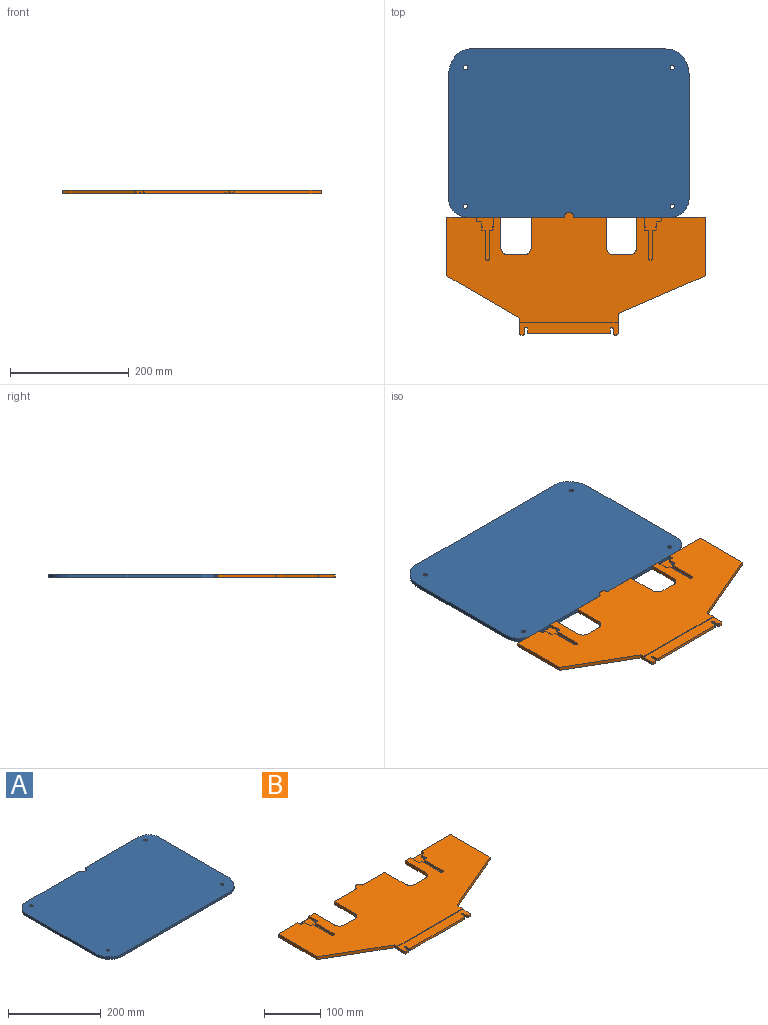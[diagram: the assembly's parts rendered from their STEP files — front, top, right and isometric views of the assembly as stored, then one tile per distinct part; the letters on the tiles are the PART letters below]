
ASSEMBLY  parts=2 mates=1
PART A: 11 faces, bbox 404x282.8x6.4 mm
  f0: extruded ~373.37x8.02mm, area 2457.8mm2, adj f1,f8,f9,f10
  f1: extruded ~271.95x18mm, area 1839.1mm2, adj f0,f2,f9,f10
  f2: extruded ~273.05x8.08mm, area 1756.8mm2, adj f1,f3,f9,f10
  f3: extruded ~94.95x6.35mm, area 609.2mm2, adj f2,f8,f9,f10
  f4: extruded ~7.5x7.5mm, area 149.3mm2, adj f9,f10
  f5: extruded ~7.5x7.5mm, area 149.3mm2, adj f9,f10
  f6: extruded ~7.5x7.5mm, area 149.3mm2, adj f9,f10
  f7: extruded ~7.5x7.5mm, area 149.3mm2, adj f9,f10
  f8: extruded ~271.86x18mm, area 1838.1mm2, adj f0,f3,f9,f10
  f9: plane 404x282.8mm, normal (0,0,1), area 113280.3mm2, adj f0,f1,f2,f3,f4,f5,f6,f7
  f10: plane 404x282.8mm, normal (0,0,-1), area 113280.3mm2, adj f0,f1,f2,f3,f4,f5,f6,f7
PART B: 92 faces, bbox 434x206x6.2 mm
  f0: plane 55.5x5.2mm, normal (0,1,0), area 288.6mm2, adj f2,f30,f77,f88
  f1: plane 114.7x5.2mm, normal (0,1,0), area 465.8mm2, adj f2,f6,f31,f38,f75,f86,f90
  f2: plane 434x184.5mm, normal (0,0,1), area 56858mm2, adj f0,f1,f4,f5,f6,f7,f8,f9
  f3: plane 434x205mm, normal (0,0,-1), area 61266.9mm2, adj f10,f11,f12,f13,f14,f15,f16,f17
  f4: plane 7.82x4.7mm, normal (1,0,0), area 36.8mm2, adj f2,f43,f72,f76
  f5: plane 15.82x4.7mm, normal (-1,0,0), area 74.4mm2, adj f2,f28,f69,f76
  f6: plane 15.82x4.7mm, normal (1,0,0), area 74.4mm2, adj f1,f2,f66,f75
  f7: plane 7.82x4.7mm, normal (-1,0,0), area 36.8mm2, adj f2,f36,f64,f75
  f8: plane 4.7x4.32mm, normal (0,1,0), area 20.3mm2, adj f2,f40,f54,f75
  f9: plane 4.7x4.32mm, normal (0,1,0), area 20.3mm2, adj f2,f47,f58,f76
  f10: plane 32.02x6.2mm, normal (1,0,0), area 171.2mm2, adj f2,f3,f12,f32,f33,f34
  f11: cylinder r=2mm len=4.8mm, axis (0,0,1), area 15.1mm2, adj f3,f25,f26,f34
  f12: cylinder r=2mm len=4.8mm, axis (0,0,1), area 15.1mm2, adj f3,f10,f13,f34
  f13: plane 4.8x4.2mm, normal (0,-1,0), area 20.2mm2, adj f3,f12,f14,f34
  f14: cylinder r=2mm len=4.8mm, axis (0,0,1), area 15.1mm2, adj f3,f13,f15,f34
  f15: plane 8.5x4.8mm, normal (-1,0,0), area 40.8mm2, adj f3,f14,f16,f34
  f16: cylinder r=2.5mm len=5mm, axis (0,0,1), area 37.7mm2, adj f3,f15,f17,f34
  f17: plane 6.5x4.8mm, normal (1,0,0), area 31.2mm2, adj f3,f16,f18,f34
  f18: cylinder r=2mm len=4.8mm, axis (0,0,1), area 15.1mm2, adj f3,f17,f19,f34
  f19: plane 134.85x4.8mm, normal (0,-1,0), area 647.3mm2, adj f3,f18,f20,f34
  f20: cylinder r=2mm len=4.8mm, axis (0,0,1), area 15.1mm2, adj f3,f19,f21,f34
  f21: plane 6.5x4.8mm, normal (-1,0,0), area 31.2mm2, adj f3,f20,f22,f34
  f22: cylinder r=2.5mm len=5mm, axis (0,0,1), area 37.7mm2, adj f3,f21,f23,f34
  f23: plane 8.5x4.8mm, normal (1,0,0), area 40.8mm2, adj f3,f22,f24,f34
  f24: cylinder r=2mm len=4.8mm, axis (0,0,1), area 15.1mm2, adj f3,f23,f25,f34
  f25: plane 4.8x4.2mm, normal (0,-1,0), area 20.2mm2, adj f3,f11,f24,f34
  f26: plane 26.41x6.2mm, normal (-1,0,0), area 136.4mm2, adj f2,f3,f11,f33,f34,f52
  f27: plane 98.79x6.2mm, normal (-1,0,0), area 612mm2, adj f2,f3,f28,f52,f87
  f28: plane 90.7x5.2mm, normal (0,1,0), area 341mm2, adj f2,f5,f27,f49,f76,f78,f87
  f29: plane 55.5x5.2mm, normal (0,1,0), area 288.6mm2, adj f2,f30,f82,f89
  f30: cylinder r=8mm len=16mm, axis (0,0,1), area 130.7mm2, adj f0,f2,f29,f91
  f31: plane 98.79x6.2mm, normal (1,0,0), area 612mm2, adj f1,f2,f3,f51,f90
  f32: cylinder r=5mm len=6.2mm, axis (0,0,1), area 14mm2, adj f2,f3,f10,f51
  f33: plane 165.25x1.4mm, normal (0,-1,0), area 231.4mm2, adj f2,f10,f26,f34
  f34: plane 165.25x21.5mm, normal (0,0,1), area 3145.4mm2, adj f10,f11,f12,f13,f14,f15,f16,f17
  f35: plane 4.7x2.14mm, normal (-1,0,0), area 10mm2, adj f2,f42,f65,f75
  f36: plane 5.5x4.7mm, normal (0,1,0), area 25.9mm2, adj f2,f7,f37,f75
  f37: cylinder r=2.5mm len=4.7mm, axis (0,0,1), area 18.5mm2, adj f2,f36,f38,f75
  f38: plane 5.5x4.7mm, normal (-1,0,0), area 25.9mm2, adj f1,f2,f37,f75
  f39: plane 4.7x2.14mm, normal (1,0,0), area 10mm2, adj f2,f40,f67,f75
  f40: cylinder r=2.5mm len=4.7mm, axis (0,0,1), area 18.5mm2, adj f2,f8,f39,f75
  f41: plane 4.7x4.32mm, normal (0,1,0), area 20.3mm2, adj f2,f42,f55,f75
  f42: cylinder r=2.5mm len=4.7mm, axis (0,0,1), area 18.5mm2, adj f2,f35,f41,f75
  f43: plane 5.5x4.7mm, normal (0,1,0), area 25.9mm2, adj f2,f4,f50,f76
  f44: plane 4.7x2.14mm, normal (1,0,0), area 10mm2, adj f2,f45,f74,f76
  f45: cylinder r=2.5mm len=4.7mm, axis (0,0,1), area 18.5mm2, adj f2,f44,f46,f76
  f46: plane 4.7x4.32mm, normal (0,1,0), area 20.3mm2, adj f2,f45,f62,f76
  f47: cylinder r=2.5mm len=4.7mm, axis (0,0,1), area 18.5mm2, adj f2,f9,f48,f76
  f48: plane 4.7x2.14mm, normal (-1,0,0), area 10mm2, adj f2,f47,f71,f76
  f49: plane 5.5x4.7mm, normal (1,0,0), area 25.9mm2, adj f2,f28,f50,f76
  f50: cylinder r=2.5mm len=4.7mm, axis (0,0,1), area 18.5mm2, adj f2,f43,f49,f76
  f51: plane 145.87x63mm, normal (0.4,-0.92,0), area 985.1mm2, adj f2,f3,f31,f32
  f52: plane 122.38x70.8mm, normal (-0.5,-0.87,0), area 876.5mm2, adj f2,f3,f26,f27
  f53: cylinder r=2mm len=4.7mm, axis (0,0,-1), area 14.8mm2, adj f2,f54,f57,f75
  f54: plane 47.61x4.7mm, normal (1,0,0), area 223.7mm2, adj f2,f8,f53,f75
  f55: plane 47.61x4.7mm, normal (-1,0,0), area 223.7mm2, adj f2,f41,f56,f75
  f56: cylinder r=2mm len=4.7mm, axis (0,0,-1), area 14.8mm2, adj f2,f55,f57,f75
  f57: plane 4.7x2.15mm, normal (0,1,0), area 10.1mm2, adj f2,f53,f56,f75
  f58: plane 47.61x4.7mm, normal (-1,0,0), area 223.7mm2, adj f2,f9,f59,f76
  f59: cylinder r=2mm len=4.7mm, axis (0,0,-1), area 14.8mm2, adj f2,f58,f60,f76
  f60: plane 4.7x2.15mm, normal (0,1,0), area 10.1mm2, adj f2,f59,f61,f76
  f61: cylinder r=2mm len=4.7mm, axis (0,0,-1), area 14.8mm2, adj f2,f60,f62,f76
  f62: plane 47.61x4.7mm, normal (1,0,0), area 223.7mm2, adj f2,f46,f61,f76
  f63: plane 4.7x2.04mm, normal (-1,0,0), area 9.6mm2, adj f2,f64,f65,f75
  f64: plane 4.7x1.53mm, normal (0,1,0), area 7.2mm2, adj f2,f7,f63,f75
  f65: plane 4.7x1.53mm, normal (0,-1,0), area 7.2mm2, adj f2,f35,f63,f75
  f66: plane 4.7x1.54mm, normal (0,1,0), area 7.2mm2, adj f2,f6,f68,f75
  f67: plane 4.7x1.54mm, normal (0,-1,0), area 7.2mm2, adj f2,f39,f68,f75
  f68: plane 4.7x2.04mm, normal (1,0,0), area 9.6mm2, adj f2,f66,f67,f75
  f69: plane 4.7x1.54mm, normal (0,1,0), area 7.2mm2, adj f2,f5,f70,f76
  f70: plane 4.7x2.04mm, normal (-1,0,0), area 9.6mm2, adj f2,f69,f71,f76
  f71: plane 4.7x1.54mm, normal (0,-1,0), area 7.2mm2, adj f2,f48,f70,f76
  f72: plane 4.7x1.53mm, normal (0,1,0), area 7.2mm2, adj f2,f4,f73,f76
  f73: plane 4.7x2.04mm, normal (1,0,0), area 9.6mm2, adj f2,f72,f74,f76
  f74: plane 4.7x1.53mm, normal (0,-1,0), area 7.2mm2, adj f2,f44,f73,f76
  f75: plane 72.11x27.8mm, normal (0,0,1), area 802.8mm2, adj f1,f6,f7,f8,f35,f36,f37,f38
  f76: plane 72.11x27.8mm, normal (0,0,1), area 802.8mm2, adj f4,f5,f9,f28,f43,f44,f45,f46
  f77: plane 50.8x6.2mm, normal (-1,0,0), area 314.5mm2, adj f0,f2,f3,f81,f88
  f78: plane 50.8x6.2mm, normal (1,0,0), area 314.5mm2, adj f2,f3,f28,f79,f87
  f79: cylinder r=12.7mm len=12.7mm, axis (0,0,1), area 123.7mm2, adj f2,f3,f78,f80
  f80: plane 25.4x6.2mm, normal (0,1,0), area 157.5mm2, adj f2,f3,f79,f81
  f81: cylinder r=12.7mm len=12.7mm, axis (0,0,1), area 123.7mm2, adj f2,f3,f77,f80
  f82: plane 50.8x6.2mm, normal (1,0,0), area 314.5mm2, adj f2,f3,f29,f83,f89
  f83: cylinder r=12.7mm len=12.7mm, axis (0,0,1), area 123.7mm2, adj f2,f3,f82,f84
  f84: plane 25.4x6.2mm, normal (0,1,0), area 157.5mm2, adj f2,f3,f83,f85
  f85: cylinder r=12.7mm len=12.7mm, axis (0,0,1), area 123.7mm2, adj f2,f3,f84,f86
  f86: plane 50.8x6.2mm, normal (-1,0,0), area 314.5mm2, adj f1,f2,f3,f85,f90
  f87: plane 90.7x1mm, normal (0,0.71,-0.71), area 128.3mm2, adj f3,f27,f28,f78
  f88: plane 56.57x1mm, normal (0,0.71,-0.71), area 79.2mm2, adj f0,f3,f77,f91
  f89: plane 56.57x1mm, normal (0,0.71,-0.71), area 79.2mm2, adj f3,f29,f82,f91
  f90: plane 114.7x1mm, normal (0,0.71,-0.71), area 162.2mm2, adj f1,f3,f31,f86
  f91: cone r=8mm half-angle=45deg, axis (0,0,1), area 34.7mm2, adj f3,f30,f88,f89
PLACE A rot(axis=(0,0,-1),180deg) t=(174.42,96.13,59.15)mm
PLACE B t=(-30.6,-243.23,60.8)mm
MATE parallel B.f2 <-> A.f9  axis (0,0,1) through (85.5,-108.73,65.5)mm
